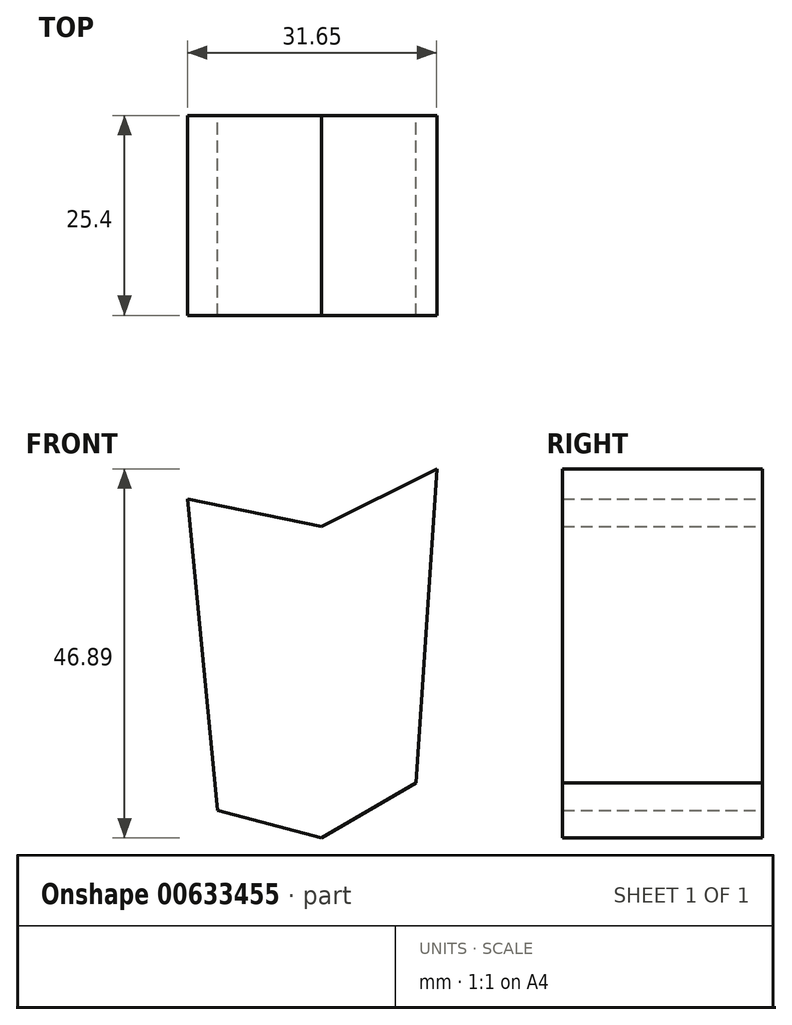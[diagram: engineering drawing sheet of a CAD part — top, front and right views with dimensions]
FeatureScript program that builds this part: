
annotation { "Feature Type Name" : "Feature", "Feature Type Description" : "" }
export const myFeature = defineFeature(function(context is Context, id is Id, definition is map)
    precondition{}
    {
        {
            var Q0;
            Q0=qCreatedBy(makeId("Front.planeOp"),FACE);
            var sketch = newSketch(context, id + "F0", { "sketchPlane" : qUnion([Q0])});
            skLineSegment(sketch, "E0", {"start": v(-3.81, 25.06) * mm, "end": v(0, -14.5) * mm});
            skLineSegment(sketch, "E1", {"start": v(0, -14.5) * mm, "end": v(13.19, -18.02) * mm});
            skLineSegment(sketch, "E2", {"start": v(13.19, -18.02) * mm, "end": v(13.19, 21.54) * mm});
            skLineSegment(sketch, "E3", {"start": v(13.19, 21.54) * mm, "end": v(-3.81, 25.06) * mm});
            skLineSegment(sketch, "E4", {"start": v(13.19, 21.54) * mm, "end": v(27.84, 28.87) * mm});
            skLineSegment(sketch, "E5", {"start": v(27.84, 28.87) * mm, "end": v(25.2, -11) * mm});
            skLineSegment(sketch, "E6", {"start": v(25.2, -11) * mm, "end": v(13.19, -18.02) * mm});
            skSolve(sketch);
        }
        {
            var Q0;
            Q0 = qSketchRegion(id + "F0", true);
            extrude(context, id + "F1", {"entities" : qUnion([Q0]), "depth" : 25.4 * mm, "offsetDistance" : 25.4 * mm});
        }
    });
